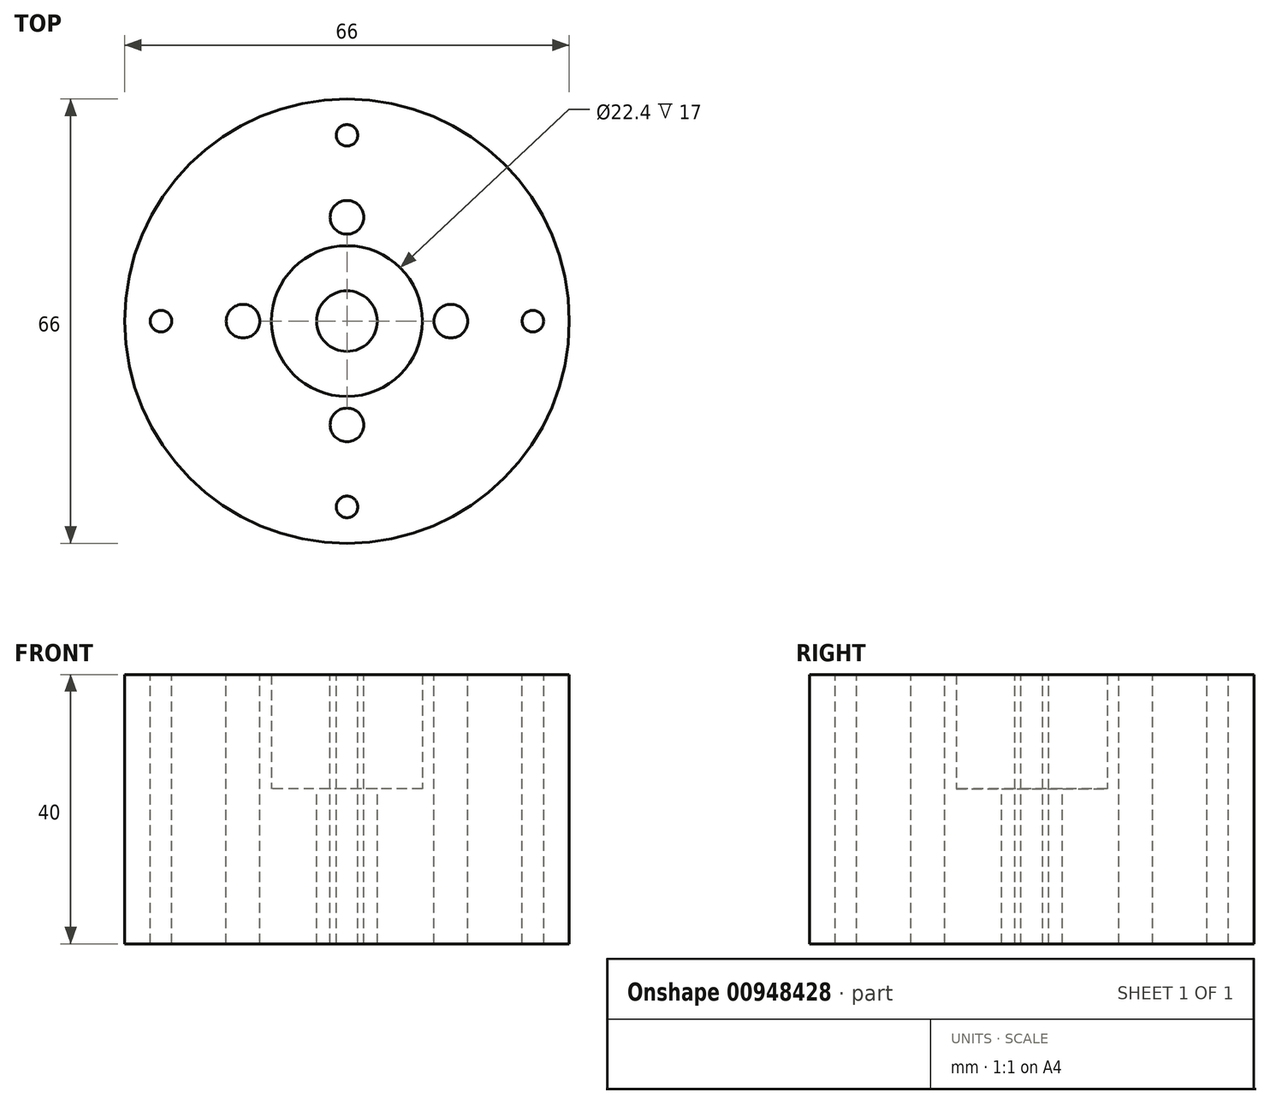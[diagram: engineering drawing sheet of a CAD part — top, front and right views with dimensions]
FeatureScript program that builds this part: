
annotation { "Feature Type Name" : "Feature", "Feature Type Description" : "" }
export const myFeature = defineFeature(function(context is Context, id is Id, definition is map)
    precondition{}
    {
        {
            var Q0;
            Q0=qCreatedBy(makeId("Top.planeOp"),FACE);
            var sketch = newSketch(context, id + "F0", { "sketchPlane" : qUnion([Q0])});
            skCircle(sketch, "E0", {"center": v(0, 0) * mm, "radius": 33 * mm});
            skCircle(sketch, "E1", {"center": v(0, 0) * mm, "radius": 11.2 * mm});
            skSolve(sketch);
        }
        {
            var Q0;
            Q0=makeQuery(id+"F0.imprint","IMPRINT",FACE,{"disambiguationData":[TD([[makeQuery(id+"F0.imprint","IMPRINT",EDGE,{"derivedFrom":sQuery(id+"F0.wireOp",EDGE,"E0")}),1.0]])]});
            var Q1;
            Q1=makeQuery(id+"F0.imprint","IMPRINT",FACE,{"disambiguationData":[TD([[makeQuery(id+"F0.imprint","IMPRINT",EDGE,{"derivedFrom":sQuery(id+"F0.wireOp",EDGE,"E1")}),1.0]])]});
            extrude(context, id + "F1", {"entities" : qUnion([Q0, Q1]), "oppositeDirection" : true, "depth" : 23 * mm, "offsetDistance" : 25 * mm});
        }
        {
            var Q0;
            Q0=makeQuery(id+"F1.opExtrude","CAP_FACE",FACE,{"disambiguationData":[OSD([sQuery(id+"F0.wireOp",EDGE,"E0")])],"isStart":true});
            var sketch = newSketch(context, id + "F2", { "sketchPlane" : qUnion([Q0])});
            skCircle(sketch, "E2", {"center": v(0, 0) * mm, "radius": 4.5 * mm});
            skSolve(sketch);
        }
        {
            var Q0;
            Q0=makeQuery(id+"F2.imprint","IMPRINT",FACE,{"disambiguationData":[TD([[makeQuery(id+"F2.imprint","IMPRINT",EDGE,{"derivedFrom":sQuery(id+"F2.wireOp",EDGE,"E2")}),1.0]])]});
            extrude(context, id + "F3", {"entities" : qUnion([Q0]), "operationType" : NewBodyOperationType.REMOVE, "endBound" : BoundingType.THROUGH_ALL, "oppositeDirection" : true, "depth" : 25 * mm, "offsetDistance" : 25 * mm});
        }
        {
            var Q0;
            Q0 = qSketchRegion(id + "F0", true);
            extrude(context, id + "F4", {"entities" : qUnion([Q0]), "operationType" : NewBodyOperationType.ADD, "depth" : 17 * mm, "offsetDistance" : 25 * mm});
        }
        {
            var Q0;
            Q0=makeQuery(id+"F4.opExtrude","CAP_FACE",FACE,{"disambiguationData":[OSD([sQuery(id+"F0.wireOp",EDGE,"E0"),sQuery(id+"F0.wireOp",EDGE,"E1")])],"isStart":false});
            var sketch = newSketch(context, id + "F5", { "sketchPlane" : qUnion([Q0])});
            skCircle(sketch, "E3", {"center": v(0, 0) * mm, "radius": 7.5 * mm});
            skCircle(sketch, "E4", {"center": v(15.42, 0) * mm, "radius": 2.5 * mm});
            skCircle(sketch, "E5.1.0", {"center": v(0, -15.42) * mm, "radius": 2.5 * mm});
            skCircle(sketch, "E5.2.0", {"center": v(-15.42, 0) * mm, "radius": 2.5 * mm});
            skCircle(sketch, "E5.3.0", {"center": v(0, 15.42) * mm, "radius": 2.5 * mm});
            skLineSegment(sketch, "E5.anchor1", {"start": v(0, 0) * mm, "end": v(15.42, 0) * mm, "construction": true});
            skLineSegment(sketch, "E5.anchor2", {"start": v(0, 0) * mm, "end": v(0, 15.42) * mm, "construction": true});
            skCircle(sketch, "E6", {"center": v(27.6, 0) * mm, "radius": 1.6 * mm});
            skCircle(sketch, "E7.1.0", {"center": v(0, 27.6) * mm, "radius": 1.6 * mm});
            skCircle(sketch, "E7.2.0", {"center": v(-27.6, 0) * mm, "radius": 1.6 * mm});
            skCircle(sketch, "E7.3.0", {"center": v(0, -27.6) * mm, "radius": 1.6 * mm});
            skSolve(sketch);
        }
        {
            var Q0;
            Q0=makeQuery(id+"F5.imprint","IMPRINT",FACE,{"disambiguationData":[TD([[makeQuery(id+"F5.imprint","IMPRINT",EDGE,{"derivedFrom":sQuery(id+"F5.wireOp",EDGE,"E4")}),1.0]])]});
            var Q1;
            Q1=makeQuery(id+"F5.imprint","IMPRINT",FACE,{"disambiguationData":[TD([[makeQuery(id+"F5.imprint","IMPRINT",EDGE,{"derivedFrom":sQuery(id+"F5.wireOp",EDGE,"E5.1.0")}),1.0]])]});
            var Q2;
            Q2=makeQuery(id+"F5.imprint","IMPRINT",FACE,{"disambiguationData":[TD([[makeQuery(id+"F5.imprint","IMPRINT",EDGE,{"derivedFrom":sQuery(id+"F5.wireOp",EDGE,"E5.3.0")}),1.0]])]});
            var Q3;
            Q3=makeQuery(id+"F5.imprint","IMPRINT",FACE,{"disambiguationData":[TD([[makeQuery(id+"F5.imprint","IMPRINT",EDGE,{"derivedFrom":sQuery(id+"F5.wireOp",EDGE,"E5.2.0")}),1.0]])]});
            var Q4;
            Q4=makeQuery(id+"F5.imprint","IMPRINT",FACE,{"disambiguationData":[TD([[makeQuery(id+"F5.imprint","IMPRINT",EDGE,{"derivedFrom":sQuery(id+"F5.wireOp",EDGE,"E6")}),1.0]])]});
            var Q5;
            Q5=makeQuery(id+"F5.imprint","IMPRINT",FACE,{"disambiguationData":[TD([[makeQuery(id+"F5.imprint","IMPRINT",EDGE,{"derivedFrom":sQuery(id+"F5.wireOp",EDGE,"E7.1.0")}),1.0]])]});
            var Q6;
            Q6=makeQuery(id+"F5.imprint","IMPRINT",FACE,{"disambiguationData":[TD([[makeQuery(id+"F5.imprint","IMPRINT",EDGE,{"derivedFrom":sQuery(id+"F5.wireOp",EDGE,"E7.3.0")}),1.0]])]});
            var Q7;
            Q7=makeQuery(id+"F5.imprint","IMPRINT",FACE,{"disambiguationData":[TD([[makeQuery(id+"F5.imprint","IMPRINT",EDGE,{"derivedFrom":sQuery(id+"F5.wireOp",EDGE,"E7.2.0")}),1.0]])]});
            var Q8;
            Q8=sQuery(id+"F5.wireOp",EDGE,"E5.1.0");
            var Q9;
            Q9=sQuery(id+"F5.wireOp",EDGE,"E4");
            var Q10;
            Q10=sQuery(id+"F5.wireOp",EDGE,"E5.3.0");
            var Q11;
            Q11=sQuery(id+"F5.wireOp",EDGE,"E5.2.0");
            extrude(context, id + "F6", {"entities" : qUnion([Q0, Q1, Q2, Q3, Q4, Q5, Q6, Q7]), "operationType" : NewBodyOperationType.REMOVE, "surfaceEntities" : qUnion([Q8, Q9, Q10, Q11]), "endBound" : BoundingType.THROUGH_ALL, "oppositeDirection" : true, "depth" : 25 * mm, "offsetDistance" : 25 * mm});
        }
    });
